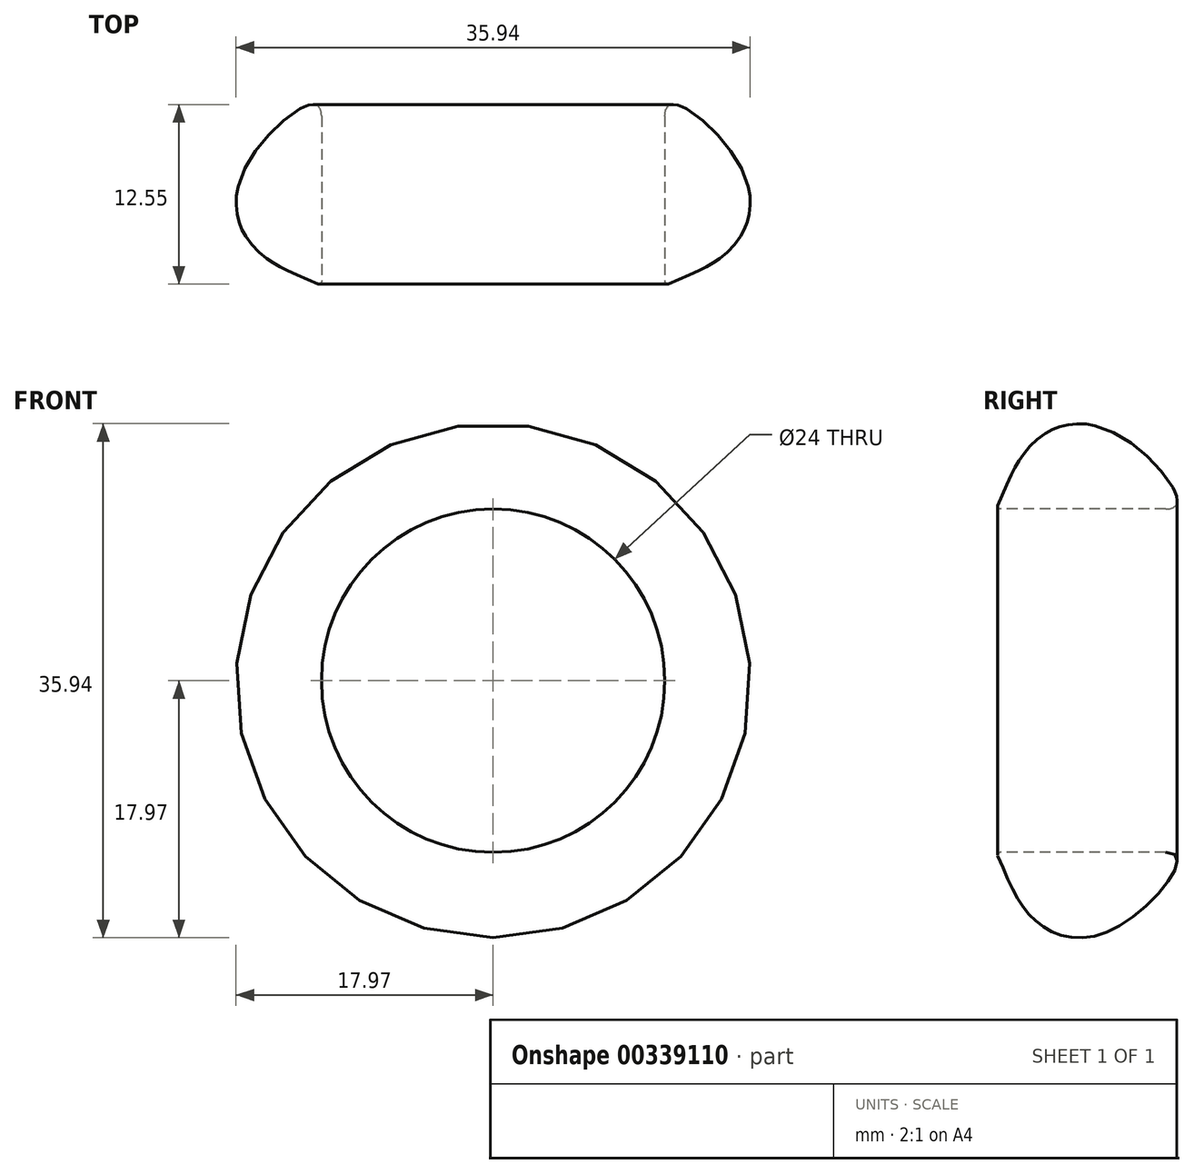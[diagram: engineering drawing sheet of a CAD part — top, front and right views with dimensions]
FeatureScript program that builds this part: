
annotation { "Feature Type Name" : "Feature", "Feature Type Description" : "" }
export const myFeature = defineFeature(function(context is Context, id is Id, definition is map)
    precondition{}
    {
        {
            var Q0;
            Q0=qCreatedBy(makeId("Top.planeOp"),FACE);
            var sketch = newSketch(context, id + "F0", { "sketchPlane" : qUnion([Q0])});
            skLineSegment(sketch, "E0", {"start": v(0, -5.79) * mm, "end": v(0, 5.79) * mm});
            skFitSpline(sketch, "E1", {"points": [v(0, 5.79) * mm, v(-5, 2.79) * mm, v(-5, -3.04) * mm, v(0, -6.04) * mm], "startDerivative": vector(0, 19.87) * mm, "endDerivative": vector(20.9, -8.64) * mm});
            skLineSegment(sketch, "E2.filletArc", {"start": v(0, 5.79) * mm, "end": v(0, 5.79) * mm});
            skArc(sketch, "E3.filletArc", {"start": v(-0.23, -5.95) * mm, "mid": v(-0.08, -5.93) * mm, "end": v(0, -5.79) * mm});
            skLineSegment(sketch, "E4", {"start": v(12, 0) * mm, "end": v(12, 6.3) * mm});
            skSolve(sketch);
        }
        {
            var Q0;
            Q0=makeQuery(id+"F0.imprint","IMPRINT",FACE,{"disambiguationData":[TD([[makeQuery(id+"F0.imprint","IMPRINT",EDGE,{"derivedFrom":sQuery(id+"F0.wireOp",EDGE,"E0")}),1.0]])]});
            var Q1;
            Q1=sQuery(id+"F0.wireOp",EDGE,"E4");
            revolve(context, id + "F1", {"entities" : qUnion([Q0]), "axis" : qUnion([Q1]), "revolveType" : RevolveType.FULL});
        }
    });
